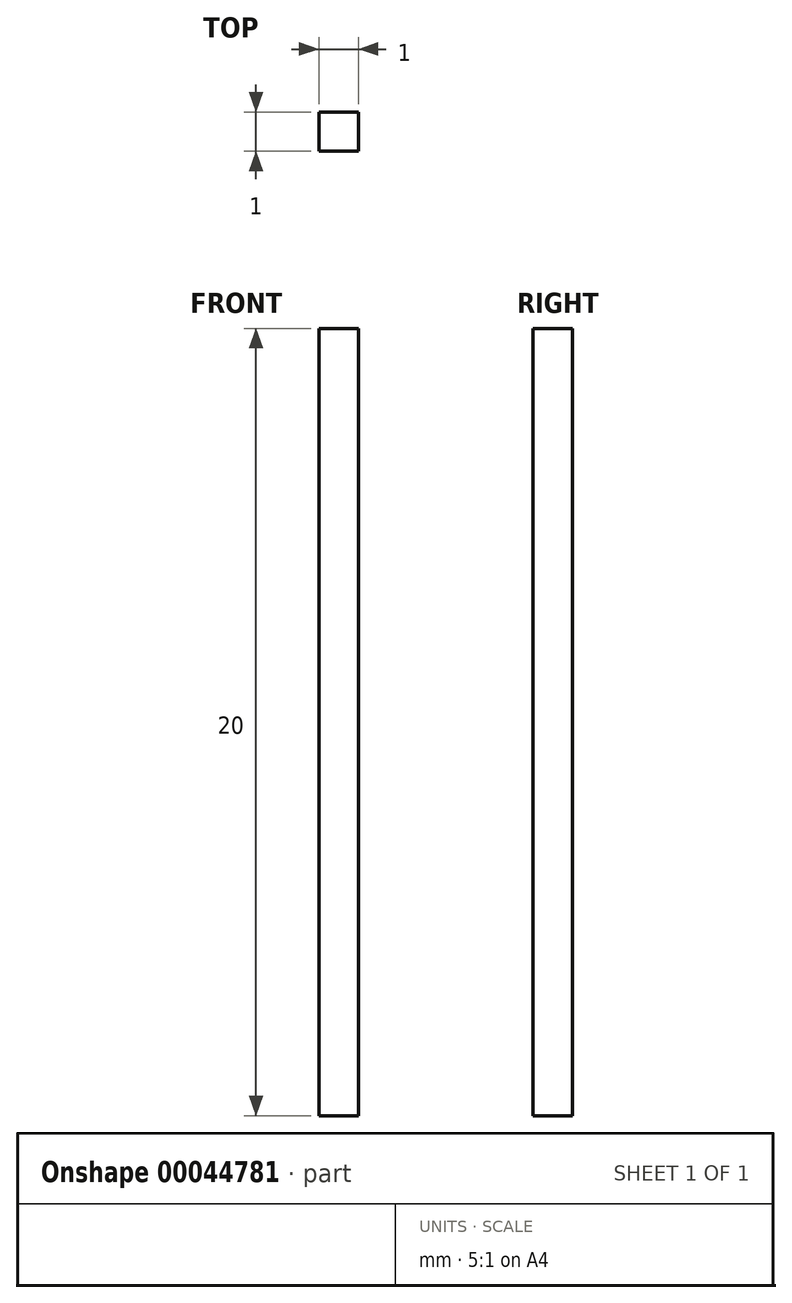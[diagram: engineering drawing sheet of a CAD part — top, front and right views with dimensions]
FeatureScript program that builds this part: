
annotation { "Feature Type Name" : "Feature", "Feature Type Description" : "" }
export const myFeature = defineFeature(function(context is Context, id is Id, definition is map)
    precondition{}
    {
        {
            var Q0;
            Q0=qCreatedBy(makeId("Front.planeOp"),FACE);
            var sketch = newSketch(context, id + "F0", { "sketchPlane" : qUnion([Q0])});
            skLineSegment(sketch, "E0.bottom", {"start": v(0, 0) * mm, "end": v(1, 0) * mm});
            skLineSegment(sketch, "E0.top", {"start": v(0, 20) * mm, "end": v(1, 20) * mm});
            skLineSegment(sketch, "E0.left", {"start": v(0, 0) * mm, "end": v(0, 20) * mm});
            skLineSegment(sketch, "E0.right", {"start": v(1, 0) * mm, "end": v(1, 20) * mm});
            skSolve(sketch);
        }
        {
            var Q0;
            Q0 = qSketchRegion(id + "F0", true);
            extrude(context, id + "F1", {"entities" : qUnion([Q0]), "depth" : 1 * mm});
        }
    });
